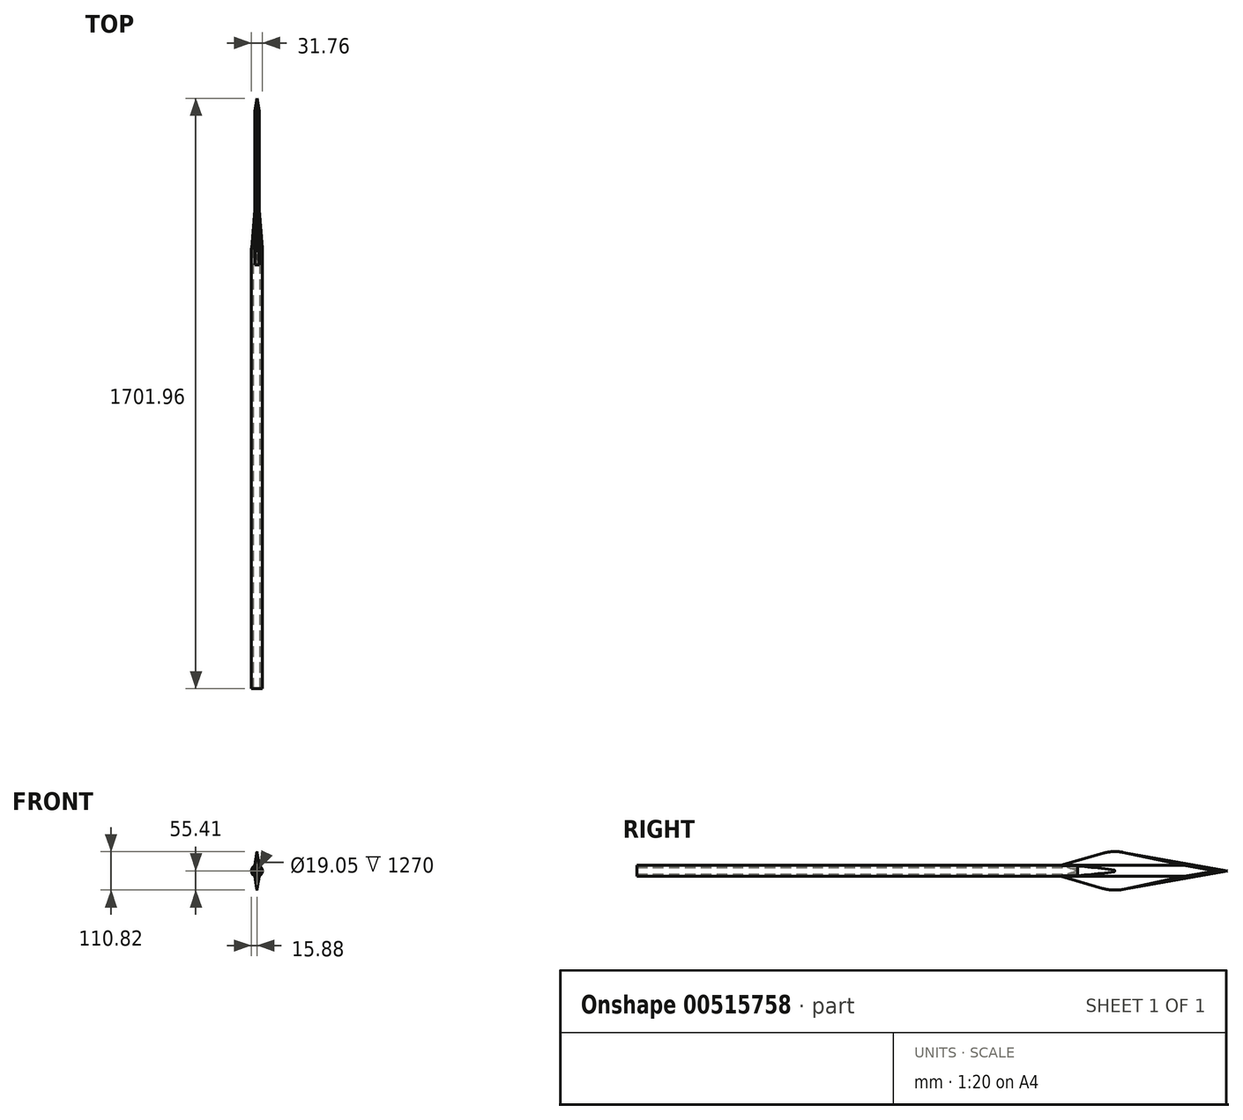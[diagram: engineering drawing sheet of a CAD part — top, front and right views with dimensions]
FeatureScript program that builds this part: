
annotation { "Feature Type Name" : "Feature", "Feature Type Description" : "" }
export const myFeature = defineFeature(function(context is Context, id is Id, definition is map)
    precondition{}
    {
        {
            var Q0;
            Q0=qCreatedBy(makeId("Front.planeOp"),FACE);
            var sketch = newSketch(context, id + "F0", { "sketchPlane" : qUnion([Q0])});
            skCircle(sketch, "E0", {"center": v(0, 0) * mm, "radius": 9.53 * mm});
            skCircle(sketch, "E1.0", {"center": v(0, 0) * mm, "radius": 15.88 * mm});
            skSolve(sketch);
        }
        {
            var Q0;
            Q0 = qSketchRegion(id + "F0", true);
            extrude(context, id + "F1", {"entities" : qUnion([Q0]), "depth" : 1270 * mm, "offsetDistance" : 25.4 * mm});
        }
        {
            var Q0;
            Q0=qCreatedBy(makeId("Right.planeOp"),FACE);
            var sketch = newSketch(context, id + "F2", { "sketchPlane" : qUnion([Q0])});
            skLineSegment(sketch, "E2", {"start": v(0, 0) * mm, "end": v(431.96, 0) * mm});
            skLineSegment(sketch, "E3", {"start": v(129.68, 53.66) * mm, "end": v(431.96, 0) * mm});
            skLineSegment(sketch, "E4", {"start": v(-48.6, 16) * mm, "end": v(72.5, 50.7) * mm});
            skLineSegment(sketch, "E5", {"start": v(0, 0) * mm, "end": v(-48.6, 16) * mm});
            skPoint(sketch, "E6.visualSharp", {"position": v(100.75, 58.8) * mm});
            skArc(sketch, "E6.filletArc", {"start": v(129.68, 53.66) * mm, "mid": v(100.92, 55.45) * mm, "end": v(72.5, 50.7) * mm});
            skLineSegment(sketch, "E7.MirrorCS", {"start": v(129.68, -53.66) * mm, "end": v(431.96, 0) * mm});
            skArc(sketch, "E8.MirrorCS", {"start": v(129.68, -53.66) * mm, "mid": v(100.92, -55.45) * mm, "end": v(72.5, -50.7) * mm});
            skLineSegment(sketch, "E9.MirrorCS", {"start": v(-48.6, -16) * mm, "end": v(72.5, -50.7) * mm});
            skLineSegment(sketch, "E10.MirrorCS", {"start": v(0, 0) * mm, "end": v(-48.6, -16) * mm});
            skSolve(sketch);
        }
        {
            var Q0;
            Q0 = qSketchRegion(id + "F2", true);
            extrude(context, id + "F3", {"entities" : qUnion([Q0]), "operationType" : NewBodyOperationType.ADD, "depth" : 6.35 * mm, "offsetDistance" : 25.4 * mm});
        }
        {
            var Q0;
            Q0=makeQuery(id+"F3.opExtrude","CAP_FACE",FACE,{"disambiguationData":[OSD([sQuery(id+"F2.wireOp",EDGE,"E3"),sQuery(id+"F2.wireOp",EDGE,"E4"),sQuery(id+"F2.wireOp",EDGE,"E5"),sQuery(id+"F2.wireOp",EDGE,"E6.filletArc"),sQuery(id+"F2.wireOp",EDGE,"E7.MirrorCS"),sQuery(id+"F2.wireOp",EDGE,"E8.MirrorCS"),sQuery(id+"F2.wireOp",EDGE,"E9.MirrorCS"),sQuery(id+"F2.wireOp",EDGE,"E10.MirrorCS")])],"isStart":true});
            var sketch = newSketch(context, id + "F4", { "sketchPlane" : qUnion([Q0])});
            skSolve(sketch);
        }
        {
            var Q0;
            {var subQ10=sQuery(id+"F2.wireOp",EDGE,"E3");Q0=makeQuery(id+"F4.imprint","IMPRINT",FACE,{"disambiguationData":[TD([[makeQuery(id+"F4.imprint","IMPRINT",EDGE,{"derivedFrom":makeQuery(id+"F3.opExtrude","CAP_EDGE",EDGE,{"disambiguationData":[OSD([subQ10])],"isStart":true})}),1.0]])]});}
            extrude(context, id + "F5", {"entities" : qUnion([Q0]), "operationType" : NewBodyOperationType.ADD, "depth" : 6.35 * mm, "offsetDistance" : 25.4 * mm});
        }
        {
            var Q0;
            Q0=qCreatedBy(makeId("Right.planeOp"),FACE);
            var sketch = newSketch(context, id + "F6", { "sketchPlane" : qUnion([Q0])});
            skLineSegment(sketch, "E11", {"start": v(0, 0) * mm, "end": v(189.09, 0) * mm});
            skLineSegment(sketch, "E12", {"start": v(189.09, 0) * mm, "end": v(0, 15.35) * mm});
            skLineSegment(sketch, "E13", {"start": v(0, 15.35) * mm, "end": v(0, 0) * mm});
            skSolve(sketch);
        }
        {
            var Q0;
            Q0 = qSketchRegion(id + "F6", true);
            var Q1;
            Q1=sQuery(id+"F6.wireOp",EDGE,"E11");
            revolve(context, id + "F7", {"operationType" : NewBodyOperationType.ADD, "entities" : qUnion([Q0]), "axis" : qUnion([Q1]), "revolveType" : RevolveType.FULL});
        }
        {
            var Q0;
            Q0=makeQuery(id+"F1.opExtrude","CAP_FACE",FACE,{"disambiguationData":[OSD([sQuery(id+"F0.wireOp",EDGE,"E0"),sQuery(id+"F0.wireOp",EDGE,"E1.0")])],"isStart":false});
            var sketch = newSketch(context, id + "F8", { "sketchPlane" : qUnion([Q0])});
            skLineSegment(sketch, "E14.0", {"start": v(-6.35, 16) * mm, "end": v(-6.35, 50.7) * mm});
            skLineSegment(sketch, "E15.0", {"start": v(-6.35, -16) * mm, "end": v(-6.35, -50.7) * mm});
            skLineSegment(sketch, "E16.0", {"start": v(6.35, 16) * mm, "end": v(6.35, 50.7) * mm});
            skLineSegment(sketch, "E17.0", {"start": v(6.35, -16) * mm, "end": v(6.35, -50.7) * mm});
            skLineSegment(sketch, "E18", {"start": v(-6.35, 16) * mm, "end": v(0, 55.4) * mm});
            skLineSegment(sketch, "E19", {"start": v(0, 55.4) * mm, "end": v(6.35, 16) * mm});
            skLineSegment(sketch, "E20", {"start": v(6.35, -16) * mm, "end": v(0, -55.4) * mm});
            skLineSegment(sketch, "E21", {"start": v(0, -55.4) * mm, "end": v(-6.35, -16) * mm});
            skLineSegment(sketch, "E22.0", {"start": v(6.35, -55.62) * mm, "end": v(6.35, -50.7) * mm});
            skLineSegment(sketch, "E23.0", {"start": v(-6.35, -55.62) * mm, "end": v(-6.35, -50.7) * mm});
            skLineSegment(sketch, "E24", {"start": v(-6.35, -55.62) * mm, "end": v(6.35, -55.62) * mm});
            skLineSegment(sketch, "E25", {"start": v(6.35, 50.7) * mm, "end": v(6.35, 55.84) * mm});
            skLineSegment(sketch, "E26", {"start": v(6.35, 55.84) * mm, "end": v(-6.51, 55.84) * mm});
            skLineSegment(sketch, "E27", {"start": v(-6.51, 55.84) * mm, "end": v(-6.35, 50.7) * mm});
            skSolve(sketch);
        }
        {
            var Q0;
            Q0 = qSketchRegion(id + "F8", true);
            extrude(context, id + "F9", {"entities" : qUnion([Q0]), "operationType" : NewBodyOperationType.REMOVE, "oppositeDirection" : true, "depth" : 1778 * mm, "offsetDistance" : 25.4 * mm});
        }
        {
            var Q0;
            Q0=makeQuery(id+"F5.opExtrude","CAP_EDGE",EDGE,{"disambiguationData":[OSD([sQuery(id+"F2.wireOp",EDGE,"E3")])],"isStart":false});
            var Q1;
            Q1=makeQuery(id+"F5.opExtrude","CAP_EDGE",EDGE,{"disambiguationData":[OSD([sQuery(id+"F2.wireOp",EDGE,"E7.MirrorCS")])],"isStart":false});
            var Q2;
            Q2=makeQuery(id+"F3.opExtrude","CAP_EDGE",EDGE,{"disambiguationData":[OSD([sQuery(id+"F2.wireOp",EDGE,"E7.MirrorCS")])],"isStart":false});
            var Q3;
            Q3=makeQuery(id+"F3.opExtrude","CAP_EDGE",EDGE,{"disambiguationData":[OSD([sQuery(id+"F2.wireOp",EDGE,"E3")])],"isStart":false});
            chamfer(context, id + "F10", {"entities" : qUnion([Q0, Q1, Q2, Q3]), "chamferType" : ChamferType.OFFSET_ANGLE, "width" : 6.35 * mm, "oppositeDirection" : false, "angle" : 45 * degree, "tangentPropagation" : true});
        }
    });
